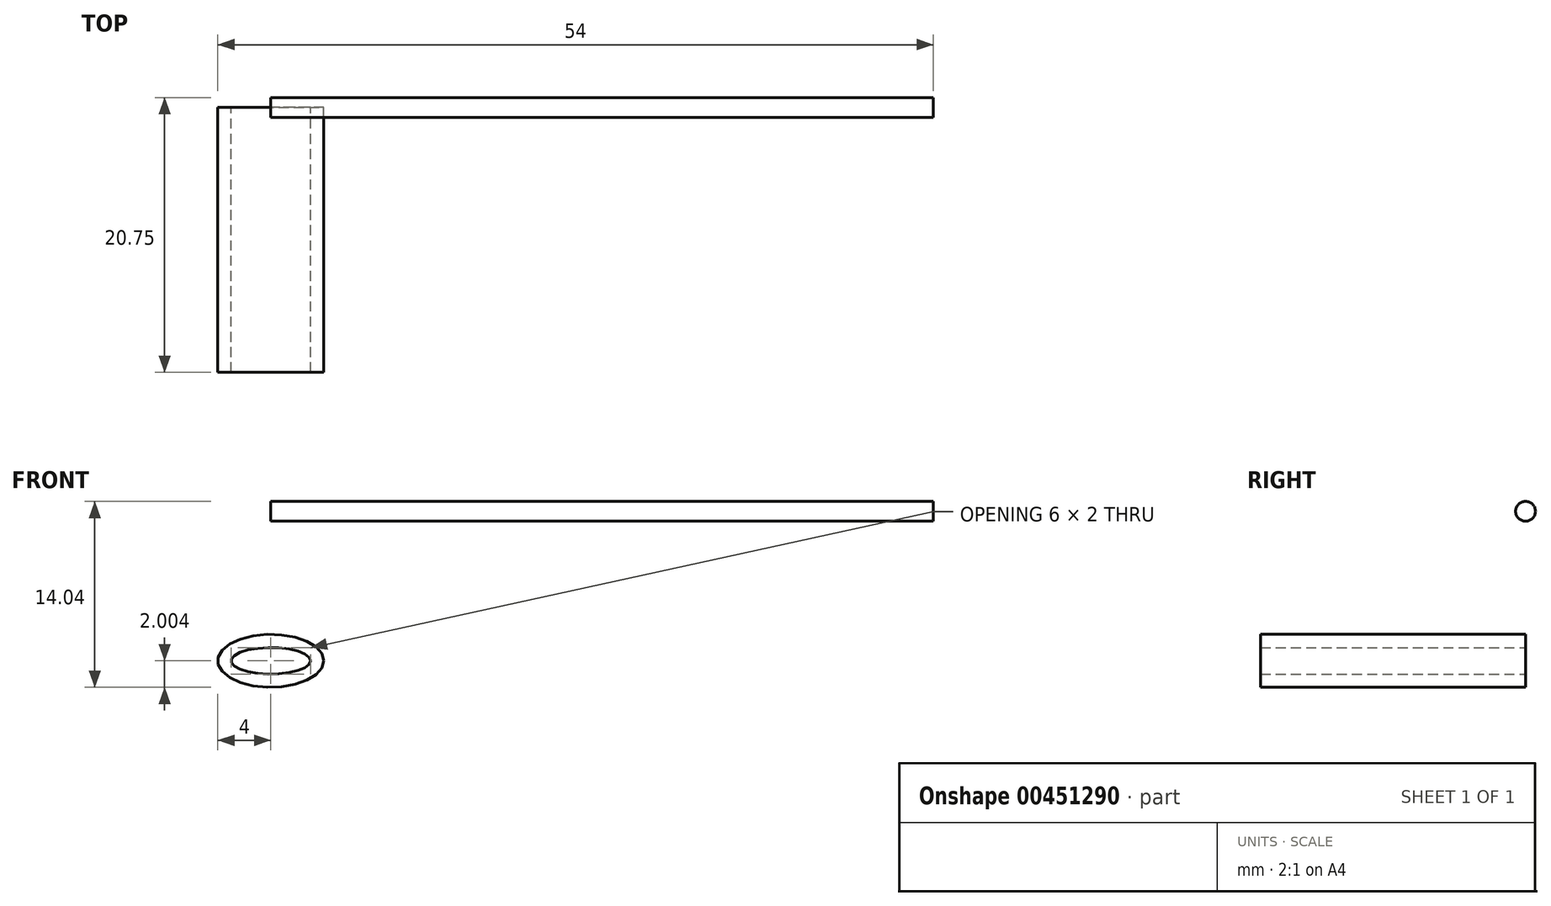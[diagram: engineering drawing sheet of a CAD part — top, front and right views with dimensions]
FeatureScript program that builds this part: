
annotation { "Feature Type Name" : "Feature", "Feature Type Description" : "" }
export const myFeature = defineFeature(function(context is Context, id is Id, definition is map)
    precondition{}
    {
        {
            var Q0;
            Q0=qCreatedBy(makeId("Front.planeOp"),FACE);
            var sketch = newSketch(context, id + "F0", { "sketchPlane" : qUnion([Q0])});
            skLineSegment(sketch, "E0", {"start": v(0, 0) * mm, "end": v(50, 0) * mm});
            skSolve(sketch);
        }
        {
            var Q0;
            Q0=qCreatedBy(makeId("Right.planeOp"),FACE);
            var sketch = newSketch(context, id + "F1", { "sketchPlane" : qUnion([Q0])});
            skCircle(sketch, "E1", {"center": v(0, 0) * mm, "radius": 0.75 * mm});
            skSolve(sketch);
        }
        {
            var Q0;
            Q0 = qSketchRegion(id + "F1", true);
            var Q1;
            Q1=sQuery(id+"F0.wireOp",EDGE,"E0");
            sweep(context, id + "F2", {"profiles" : qUnion([Q0]), "path" : qUnion([Q1])});
        }
        {
            var Q0;
            Q0=qCreatedBy(makeId("Front.planeOp"),FACE);
            var sketch = newSketch(context, id + "F3", { "sketchPlane" : qUnion([Q0])});
            skEllipse(sketch, "E2", {"center": v(0, -11.29) * mm, "majorRadius": 3 * mm, "minorRadius": 1 * mm, "majorAxis": v(1, 0)});
            skEllipse(sketch, "E3", {"center": v(0, -11.29) * mm, "majorRadius": 4 * mm, "minorRadius": 2 * mm, "majorAxis": v(1, 0)});
            skSolve(sketch);
        }
        {
            var Q0;
            Q0 = qSketchRegion(id + "F3", true);
            extrude(context, id + "F4", {"entities" : qUnion([Q0]), "depth" : 20 * mm});
        }
    });
